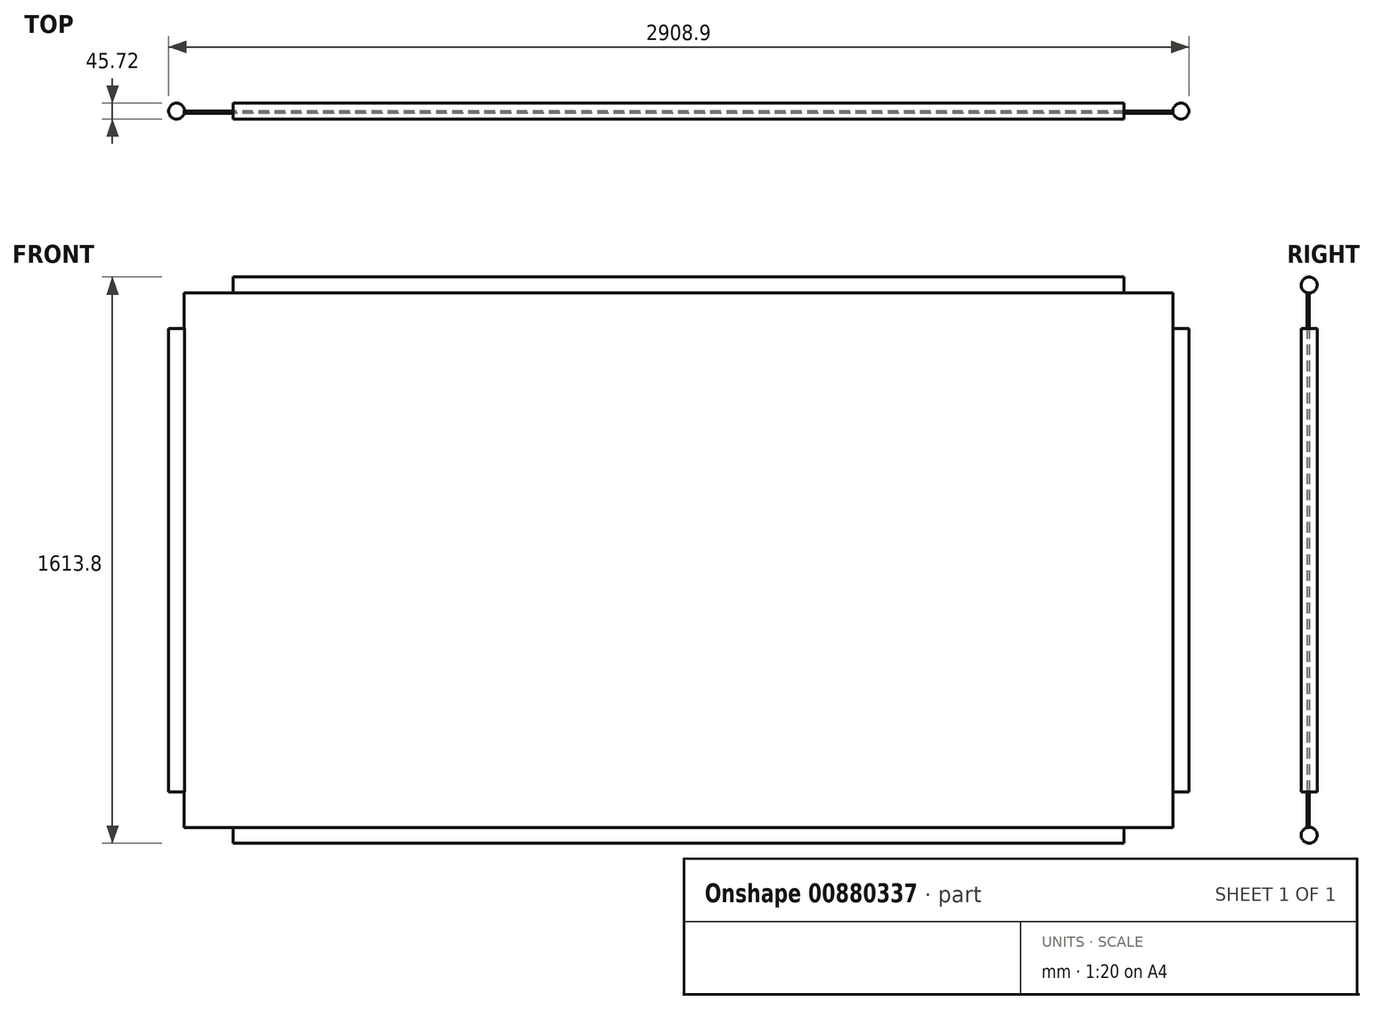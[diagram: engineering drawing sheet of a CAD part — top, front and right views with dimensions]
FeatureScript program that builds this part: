
annotation { "Feature Type Name" : "Feature", "Feature Type Description" : "" }
export const myFeature = defineFeature(function(context is Context, id is Id, definition is map)
    precondition{}
    {
        {
            var Q0;
            Q0=qCreatedBy(makeId("Front.planeOp"),FACE);
            var sketch = newSketch(context, id + "F0", { "sketchPlane" : qUnion([Q0])});
            skLineSegment(sketch, "E0.bottom", {"start": v(1409.7, 762) * mm, "end": v(-1409.7, 762) * mm});
            skLineSegment(sketch, "E0.top", {"start": v(1409.7, -762) * mm, "end": v(-1409.7, -762) * mm});
            skLineSegment(sketch, "E0.left", {"start": v(1409.7, 762) * mm, "end": v(1409.7, -762) * mm});
            skLineSegment(sketch, "E0.right", {"start": v(-1409.7, 762) * mm, "end": v(-1409.7, -762) * mm});
            skPoint(sketch, "E0.middle", {"position": v(0, 0) * mm});
            skSolve(sketch);
        }
        {
            var Q0;
            Q0=qCreatedBy(makeId("Right.planeOp"),FACE);
            var sketch = newSketch(context, id + "F1", { "sketchPlane" : qUnion([Q0])});
            skCircle(sketch, "E1", {"center": v(0, 783.91) * mm, "radius": 22.86 * mm});
            skCircle(sketch, "E2", {"center": v(0, -784.17) * mm, "radius": 22.86 * mm});
            skSolve(sketch);
        }
        {
            var Q0;
            Q0=makeQuery(id+"F0.imprint","IMPRINT",FACE,{"disambiguationData":[TD([[makeQuery(id+"F0.imprint","IMPRINT",EDGE,{"derivedFrom":sQuery(id+"F0.wireOp",EDGE,"E0.bottom")}),1.0]])]});
            extrude(context, id + "F2", {"entities" : qUnion([Q0]), "depth" : 6.35 * mm, "offsetDistance" : 25.4 * mm});
        }
        {
            var Q0;
            Q0 = qSketchRegion(id + "F1", true);
            extrude(context, id + "F3", {"entities" : qUnion([Q0]), "operationType" : NewBodyOperationType.ADD, "endBound" : BoundingType.SYMMETRIC, "depth" : 2540 * mm, "offsetDistance" : 25.4 * mm});
        }
        {
            var Q0;
            Q0=qCreatedBy(makeId("Top.planeOp"),FACE);
            var sketch = newSketch(context, id + "F4", { "sketchPlane" : qUnion([Q0])});
            skCircle(sketch, "E3", {"center": v(-1431.52, 0) * mm, "radius": 22.86 * mm});
            skCircle(sketch, "E4", {"center": v(1431.66, 0) * mm, "radius": 22.86 * mm});
            skSolve(sketch);
        }
        {
            var Q0;
            Q0 = qSketchRegion(id + "F4", true);
            extrude(context, id + "F5", {"entities" : qUnion([Q0]), "operationType" : NewBodyOperationType.ADD, "endBound" : BoundingType.SYMMETRIC, "depth" : 1320.8 * mm, "offsetDistance" : 25.4 * mm});
        }
    });
